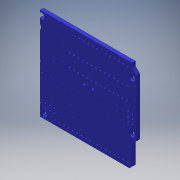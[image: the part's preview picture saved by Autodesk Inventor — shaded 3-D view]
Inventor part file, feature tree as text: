
AUTODESK INVENTOR PART (.ipt)
format: ipt  version: 2016 (Build 200138000, 138)  size: 839,680 bytes
history: native  units: mm
features: other x1, imported_body x1, extrude x1, sketch x1
ambient origin geometry x8: Origin, YZ Plane, XZ Plane, XY Plane, X Axis, Y Axis, Z Axis, Center Point
bodies: Body1 (feature_tree)
feature tree (4):
  other  "Cortar-Extruir2"
  imported_body  "Base1"
  extrude  "Extrusion1"  Depth=10.0mm TaperAngle=0.0deg
  sketch  "Sketch1"  dims[d0=13.0mm d1=10.0mm d2=0.0mm]
